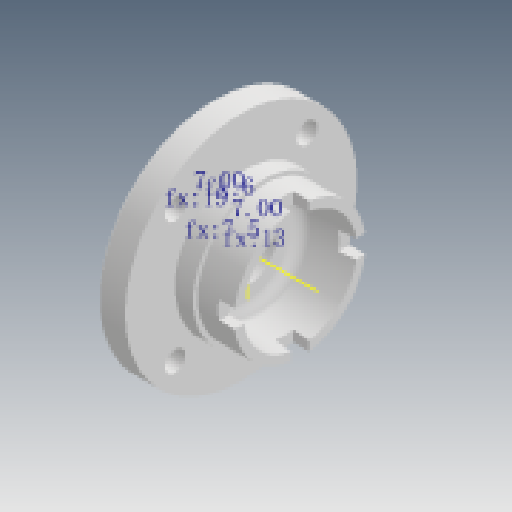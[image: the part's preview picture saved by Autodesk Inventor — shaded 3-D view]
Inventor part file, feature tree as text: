
AUTODESK INVENTOR PART (.ipt)
format: ipt  version: 2025 (Build 290162000, 162)  size: 430,592 bytes
history: native  units: in
note: dims shown in document units (in); Inventor stores cm internally (conversion verified against a paired STEP export)
features: sketch x6, extrude x3, revolve x2, chamfer x1, fillet x1
ambient origin geometry x8: Origin, YZ Plane, XZ Plane, XY Plane, X Axis, Y Axis, Z Axis, Center Point
bodies: 实体1 (feature_tree)
feature tree (13):
  revolve  "旋转1"  [1 undecoded]
  extrude  "拉伸1"  Depth=0.4724in
  extrude  "拉伸2"  Depth=1.1417in
  extrude  "拉伸3"  Depth=0.3937in
  chamfer  "倒角1"  Distance=0.0394in
  fillet  "圆角1"  Radius=0.5906in
  sketch  "草图5"  dims[d11=45.0deg d12=0.0394in d13=0.5906in d14=0.9843in d15=0.5792in d16=90.0deg d17=0.2756in d18=0.315in d19=0.0in d20=0.2756in d21=0.315in d22=0.0in d23=0.3543in d24=1.6142in d25=1.5748in d27=360.0deg d29=0.315in d30=0.0in d31=0.0394in d32=0.0787in d33=45.0deg d34=0.1969in d35=0.5118in d36=0.748in d37=0.2362in d38=0.0481in d39=0.0481in d40=0.2953in d41=90.0deg d42=45.0deg]
  revolve  "旋转2"  [1 undecoded]
  sketch  "草图1"  dims[d3=0.315in d0=0.3543in d1=1.0236in d2=2.0079in]
  sketch  "草图2"  dims[d6=1.2205in d7=1.1417in]
  sketch  "草图3"  dims[d8=0.3937in d9=0.0984in]
  sketch  "草图4"  dims[d10=1.1417in]
  sketch  "草图 - 环形阵列1"  dims[d4=1.0236in d5=0.4724in]
note: 2 required parameter values undecoded (feature->parameter linkage not recoverable at this tier; creation-order binding heuristic only, values carry confidence <= 0.55)
